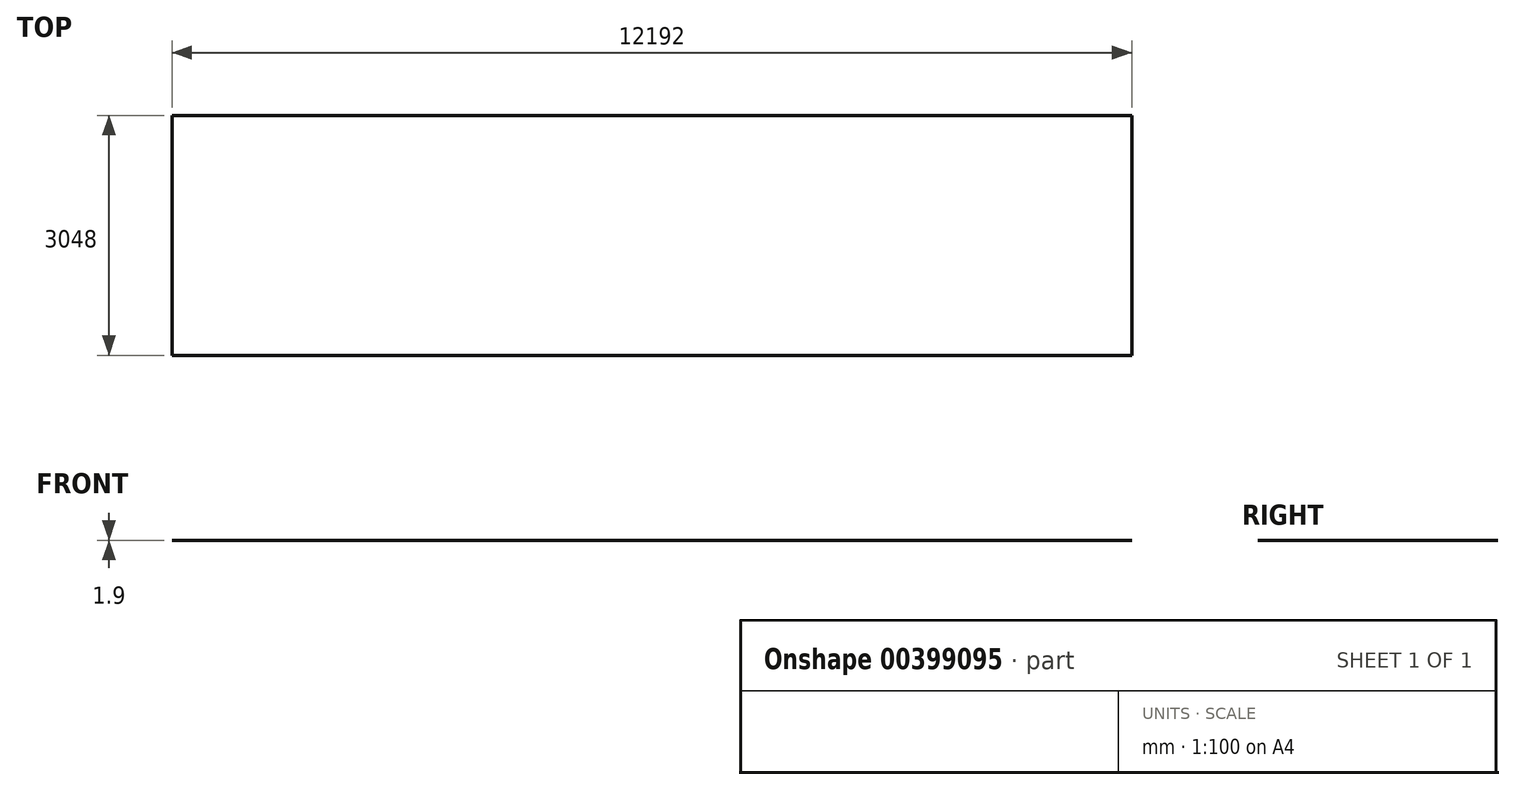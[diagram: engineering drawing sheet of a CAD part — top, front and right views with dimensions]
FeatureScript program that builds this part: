
annotation { "Feature Type Name" : "Feature", "Feature Type Description" : "" }
export const myFeature = defineFeature(function(context is Context, id is Id, definition is map)
    precondition{}
    {
        {
            var Q0;
            Q0=qCreatedBy(makeId("Top.planeOp"),FACE);
            var sketch = newSketch(context, id + "F0", { "sketchPlane" : qUnion([Q0])});
            skLineSegment(sketch, "E0.bottom", {"start": v(-6095.9, 0) * mm, "end": v(6096.1, 0) * mm});
            skLineSegment(sketch, "E0.top", {"start": v(-6095.9, -3048) * mm, "end": v(6096.1, -3048) * mm});
            skLineSegment(sketch, "E0.left", {"start": v(-6095.9, 0) * mm, "end": v(-6095.9, -3048) * mm});
            skLineSegment(sketch, "E0.right", {"start": v(6096.1, 0) * mm, "end": v(6096.1, -3048) * mm});
            skSolve(sketch);
        }
        {
            var Q0;
            Q0=makeQuery(id+"F0.imprint","IMPRINT",FACE,{"disambiguationData":[TD([[makeQuery(id+"F0.imprint","IMPRINT",EDGE,{"derivedFrom":sQuery(id+"F0.wireOp",EDGE,"E0.bottom")}),-1.0]])]});
            extrude(context, id + "F1", {"entities" : qUnion([Q0]), "oppositeDirection" : true, "depth" : 1.9 * mm});
        }
    });
